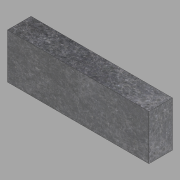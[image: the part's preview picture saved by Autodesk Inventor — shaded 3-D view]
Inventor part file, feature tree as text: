
AUTODESK INVENTOR PART (.ipt)
format: ipt  version: 2022.1 (Build 261234020, 234B)  size: 119,296 bytes
history: native  units: in
note: dims shown in document units (in); Inventor stores cm internally (conversion verified against a paired STEP export)
features: extrude x1, sketch x1
ambient origin geometry x8: Origin, YZ Plane, XZ Plane, XY Plane, X Axis, Y Axis, Z Axis, Center Point
bodies: Solid1 (feature_tree)
feature tree (2):
  extrude  "Extrusion1"  Depth=11.5in
  sketch  "Sketch1"  dims[d0=36.0in d1=11.5in d2=6.0in d3=0.0in]
